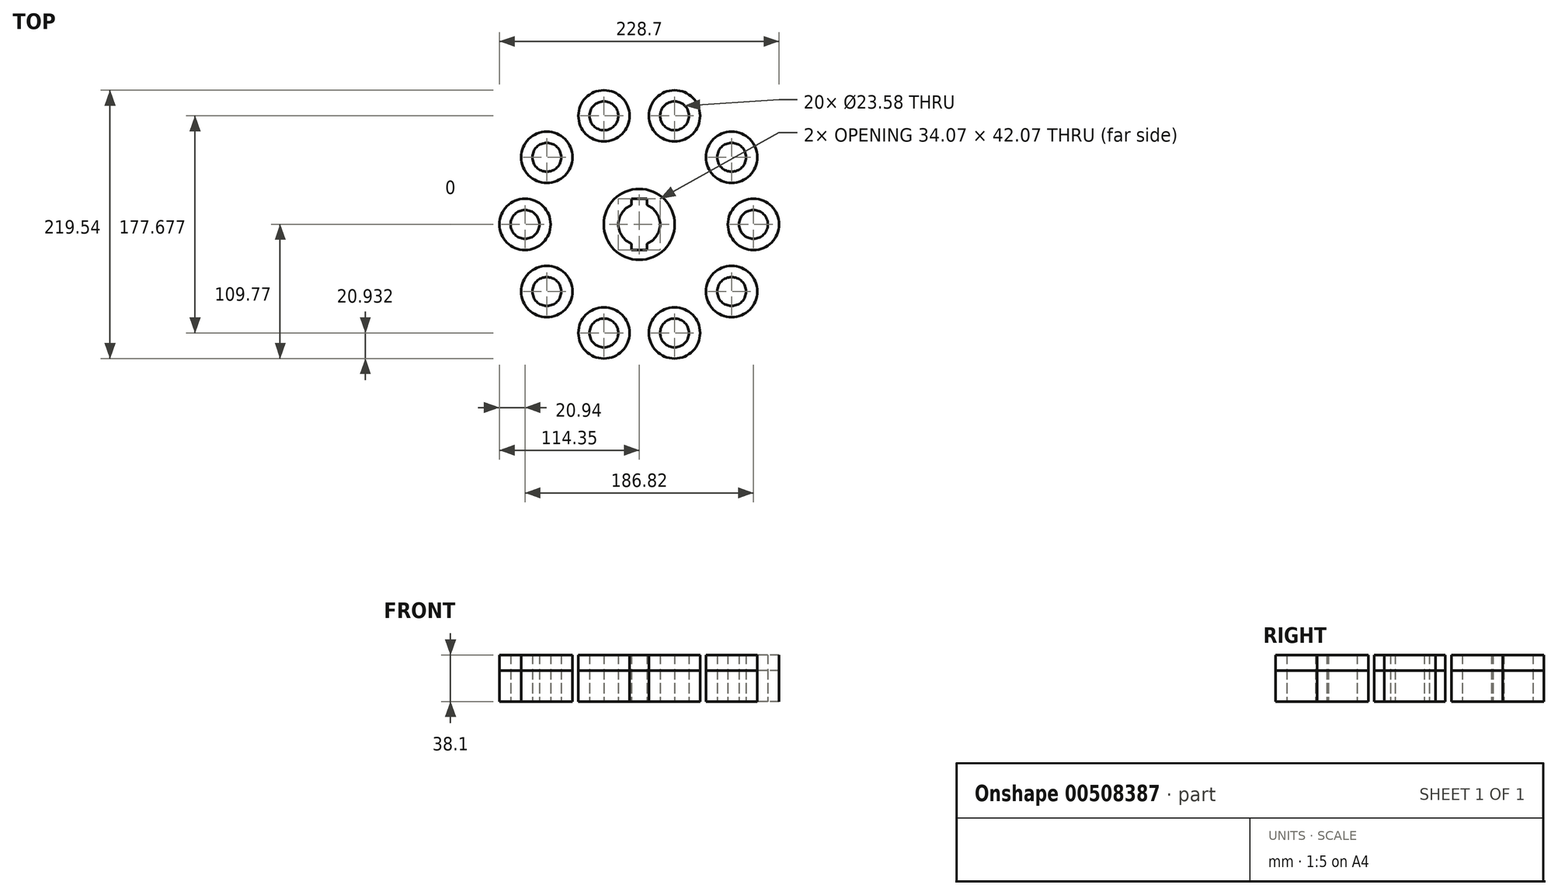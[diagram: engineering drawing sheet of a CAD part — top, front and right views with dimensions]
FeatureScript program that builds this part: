
annotation { "Feature Type Name" : "Feature", "Feature Type Description" : "" }
export const myFeature = defineFeature(function(context is Context, id is Id, definition is map)
    precondition{}
    {
        {
            var Q0;
            Q0=qCreatedBy(makeId("Top.planeOp"),FACE);
            var sketch = newSketch(context, id + "F0", { "sketchPlane" : qUnion([Q0])});
            skCircle(sketch, "E0", {"center": v(0, 0) * mm, "radius": 29.02 * mm});
            skCircle(sketch, "E1", {"center": v(-93.41, 0) * mm, "radius": 20.94 * mm});
            skCircle(sketch, "E2.1.1", {"center": v(-75.57, -54.9) * mm, "radius": 20.94 * mm});
            skCircle(sketch, "E2.2.1", {"center": v(-28.87, -88.84) * mm, "radius": 20.94 * mm});
            skCircle(sketch, "E2.3.1", {"center": v(28.87, -88.84) * mm, "radius": 20.94 * mm});
            skCircle(sketch, "E2.4.1", {"center": v(75.57, -54.9) * mm, "radius": 20.94 * mm});
            skCircle(sketch, "E2.5.1", {"center": v(93.41, 0) * mm, "radius": 20.94 * mm});
            skCircle(sketch, "E2.6.1", {"center": v(75.57, 54.9) * mm, "radius": 20.94 * mm});
            skCircle(sketch, "E2.7.1", {"center": v(28.87, 88.84) * mm, "radius": 20.94 * mm});
            skCircle(sketch, "E2.8.1", {"center": v(-28.87, 88.84) * mm, "radius": 20.94 * mm});
            skCircle(sketch, "E2.9.1", {"center": v(-75.57, 54.9) * mm, "radius": 20.94 * mm});
            skCircle(sketch, "E3", {"center": v(-93.41, 0) * mm, "radius": 11.8 * mm});
            skCircle(sketch, "E4.1.0", {"center": v(-75.57, -54.9) * mm, "radius": 11.8 * mm});
            skCircle(sketch, "E4.2.0", {"center": v(-28.87, -88.84) * mm, "radius": 11.8 * mm});
            skCircle(sketch, "E4.3.0", {"center": v(28.87, -88.84) * mm, "radius": 11.8 * mm});
            skCircle(sketch, "E4.4.0", {"center": v(75.57, -54.9) * mm, "radius": 11.8 * mm});
            skCircle(sketch, "E4.5.0", {"center": v(93.41, 0) * mm, "radius": 11.8 * mm});
            skCircle(sketch, "E4.6.0", {"center": v(75.57, 54.9) * mm, "radius": 11.8 * mm});
            skCircle(sketch, "E4.7.0", {"center": v(28.87, 88.84) * mm, "radius": 11.8 * mm});
            skCircle(sketch, "E4.8.0", {"center": v(-28.87, 88.84) * mm, "radius": 11.8 * mm});
            skCircle(sketch, "E4.9.0", {"center": v(-75.57, 54.9) * mm, "radius": 11.8 * mm});
            skArc(sketch, "E5", {"start": v(-6.2, 15.86) * mm, "mid": v(-17.04, 0) * mm, "end": v(-6.2, -15.86) * mm});
            skLineSegment(sketch, "E6.bottom", {"start": v(-6.2, 21.03) * mm, "end": v(6.2, 21.03) * mm});
            skLineSegment(sketch, "E6.top", {"start": v(-6.2, -21.03) * mm, "end": v(6.2, -21.03) * mm});
            skLineSegment(sketch, "E6.left", {"start": v(-6.2, 21.03) * mm, "end": v(-6.2, 15.86) * mm});
            skLineSegment(sketch, "E6.right", {"start": v(6.2, 21.03) * mm, "end": v(6.2, 15.86) * mm});
            skLineSegment(sketch, "E7.trimOffspring", {"start": v(43.7, -60.1) * mm, "end": v(64.74, -72.82) * mm});
            skLineSegment(sketch, "E8.trimOffspring", {"start": v(0.02, -74.3) * mm, "end": v(-9.57, -96.97) * mm});
            skLineSegment(sketch, "E9.trimOffspring", {"start": v(43.7, -60.1) * mm, "end": v(49.25, -84.08) * mm});
            skLineSegment(sketch, "E10.trimOffspring", {"start": v(70.67, -22.94) * mm, "end": v(95.18, -20.86) * mm});
            skLineSegment(sketch, "E11.trimOffspring", {"start": v(70.66, 22.98) * mm, "end": v(89.27, 39.07) * mm});
            skLineSegment(sketch, "E12.trimOffspring", {"start": v(0.02, -74.3) * mm, "end": v(9.57, -96.97) * mm});
            skLineSegment(sketch, "E13.trimOffspring", {"start": v(-43.66, -60.13) * mm, "end": v(-49.25, -84.08) * mm});
            skLineSegment(sketch, "E14.trimOffspring", {"start": v(-43.66, -60.13) * mm, "end": v(-64.74, -72.82) * mm});
            skLineSegment(sketch, "E15.trimOffspring", {"start": v(-70.66, -22.98) * mm, "end": v(-95.18, -20.86) * mm});
            skLineSegment(sketch, "E16.trimOffspring", {"start": v(-70.66, -22.98) * mm, "end": v(-89.27, -39.07) * mm});
            skLineSegment(sketch, "E17.trimOffspring", {"start": v(-70.67, 22.94) * mm, "end": v(-89.27, 39.07) * mm});
            skLineSegment(sketch, "E18.trimOffspring", {"start": v(-70.67, 22.94) * mm, "end": v(-95.18, 20.86) * mm});
            skLineSegment(sketch, "E19.trimOffspring", {"start": v(-43.7, 60.1) * mm, "end": v(-49.25, 84.08) * mm});
            skLineSegment(sketch, "E20.trimOffspring", {"start": v(-0.02, 74.3) * mm, "end": v(9.57, 96.97) * mm});
            skLineSegment(sketch, "E21.trimOffspring", {"start": v(-43.7, 60.1) * mm, "end": v(-64.74, 72.82) * mm});
            skLineSegment(sketch, "E22.trimOffspring", {"start": v(-0.02, 74.3) * mm, "end": v(-9.57, 96.97) * mm});
            skLineSegment(sketch, "E23.trimOffspring", {"start": v(43.66, 60.13) * mm, "end": v(64.74, 72.82) * mm});
            skLineSegment(sketch, "E24.trimOffspring", {"start": v(43.66, 60.13) * mm, "end": v(49.25, 84.08) * mm});
            skLineSegment(sketch, "E25.trimOffspring", {"start": v(70.66, 22.98) * mm, "end": v(95.18, 20.86) * mm});
            skLineSegment(sketch, "E26.trimOffspring", {"start": v(70.67, -22.94) * mm, "end": v(89.27, -39.07) * mm});
            skPoint(sketch, "E27.orphan", {"position": v(28.58, 5.08) * mm});
            skLineSegment(sketch, "E28.trimOffspring", {"start": v(6.2, -15.86) * mm, "end": v(6.2, -21.03) * mm});
            skLineSegment(sketch, "E29.trimOffspring", {"start": v(-6.2, -15.86) * mm, "end": v(-6.2, -21.03) * mm});
            skArc(sketch, "E30.trimOffspring", {"start": v(6.2, -15.86) * mm, "mid": v(17.04, 0) * mm, "end": v(6.2, 15.86) * mm});
            skPoint(sketch, "E31.orphan", {"position": v(-28.58, -5.08) * mm});
            skPoint(sketch, "E32.orphan", {"position": v(-28.82, 3.4) * mm});
            skSolve(sketch);
        }
        {
            var Q0;
            Q0=makeQuery(id+"F0.imprint","IMPRINT",FACE,{"disambiguationData":[TD([[makeQuery(id+"F0.imprint","IMPRINT",EDGE,{"derivedFrom":sQuery(id+"F0.wireOp",EDGE,"E4.9.0")}),-1.0]])]});
            var Q1;
            Q1=makeQuery(id+"F0.imprint","IMPRINT",FACE,{"disambiguationData":[TD([[makeQuery(id+"F0.imprint","IMPRINT",EDGE,{"derivedFrom":sQuery(id+"F0.wireOp",EDGE,"E3")}),-1.0]])]});
            var Q2;
            Q2=makeQuery(id+"F0.imprint","IMPRINT",FACE,{"disambiguationData":[TD([[makeQuery(id+"F0.imprint","IMPRINT",EDGE,{"derivedFrom":sQuery(id+"F0.wireOp",EDGE,"E4.1.0")}),-1.0]])]});
            var Q3;
            Q3=makeQuery(id+"F0.imprint","IMPRINT",FACE,{"disambiguationData":[TD([[makeQuery(id+"F0.imprint","IMPRINT",EDGE,{"derivedFrom":sQuery(id+"F0.wireOp",EDGE,"E4.2.0")}),-1.0]])]});
            var Q4;
            Q4=makeQuery(id+"F0.imprint","IMPRINT",FACE,{"disambiguationData":[TD([[makeQuery(id+"F0.imprint","IMPRINT",EDGE,{"derivedFrom":sQuery(id+"F0.wireOp",EDGE,"E4.3.0")}),-1.0]])]});
            var Q5;
            Q5=makeQuery(id+"F0.imprint","IMPRINT",FACE,{"disambiguationData":[TD([[makeQuery(id+"F0.imprint","IMPRINT",EDGE,{"derivedFrom":sQuery(id+"F0.wireOp",EDGE,"E4.4.0")}),-1.0]])]});
            var Q6;
            Q6=makeQuery(id+"F0.imprint","IMPRINT",FACE,{"disambiguationData":[TD([[makeQuery(id+"F0.imprint","IMPRINT",EDGE,{"derivedFrom":sQuery(id+"F0.wireOp",EDGE,"E4.5.0")}),-1.0]])]});
            var Q7;
            Q7=makeQuery(id+"F0.imprint","IMPRINT",FACE,{"disambiguationData":[TD([[makeQuery(id+"F0.imprint","IMPRINT",EDGE,{"derivedFrom":sQuery(id+"F0.wireOp",EDGE,"E0")}),1.0]])]});
            var Q8;
            Q8=makeQuery(id+"F0.imprint","IMPRINT",FACE,{"disambiguationData":[TD([[makeQuery(id+"F0.imprint","IMPRINT",EDGE,{"derivedFrom":sQuery(id+"F0.wireOp",EDGE,"E4.6.0")}),-1.0]])]});
            var Q9;
            Q9=makeQuery(id+"F0.imprint","IMPRINT",FACE,{"disambiguationData":[TD([[makeQuery(id+"F0.imprint","IMPRINT",EDGE,{"derivedFrom":sQuery(id+"F0.wireOp",EDGE,"E4.7.0")}),-1.0]])]});
            var Q10;
            Q10=makeQuery(id+"F0.imprint","IMPRINT",FACE,{"disambiguationData":[TD([[makeQuery(id+"F0.imprint","IMPRINT",EDGE,{"derivedFrom":sQuery(id+"F0.wireOp",EDGE,"E4.8.0")}),-1.0]])]});
            extrude(context, id + "F1", {"entities" : qUnion([Q0, Q1, Q2, Q3, Q4, Q5, Q6, Q7, Q8, Q9, Q10]), "depth" : 38.1 * mm});
        }
        {
            var Q0;
            Q0 = qSketchRegion(id + "F0", true);
            extrude(context, id + "F2", {"entities" : qUnion([Q0]), "depth" : 25.4 * mm});
        }
    });
